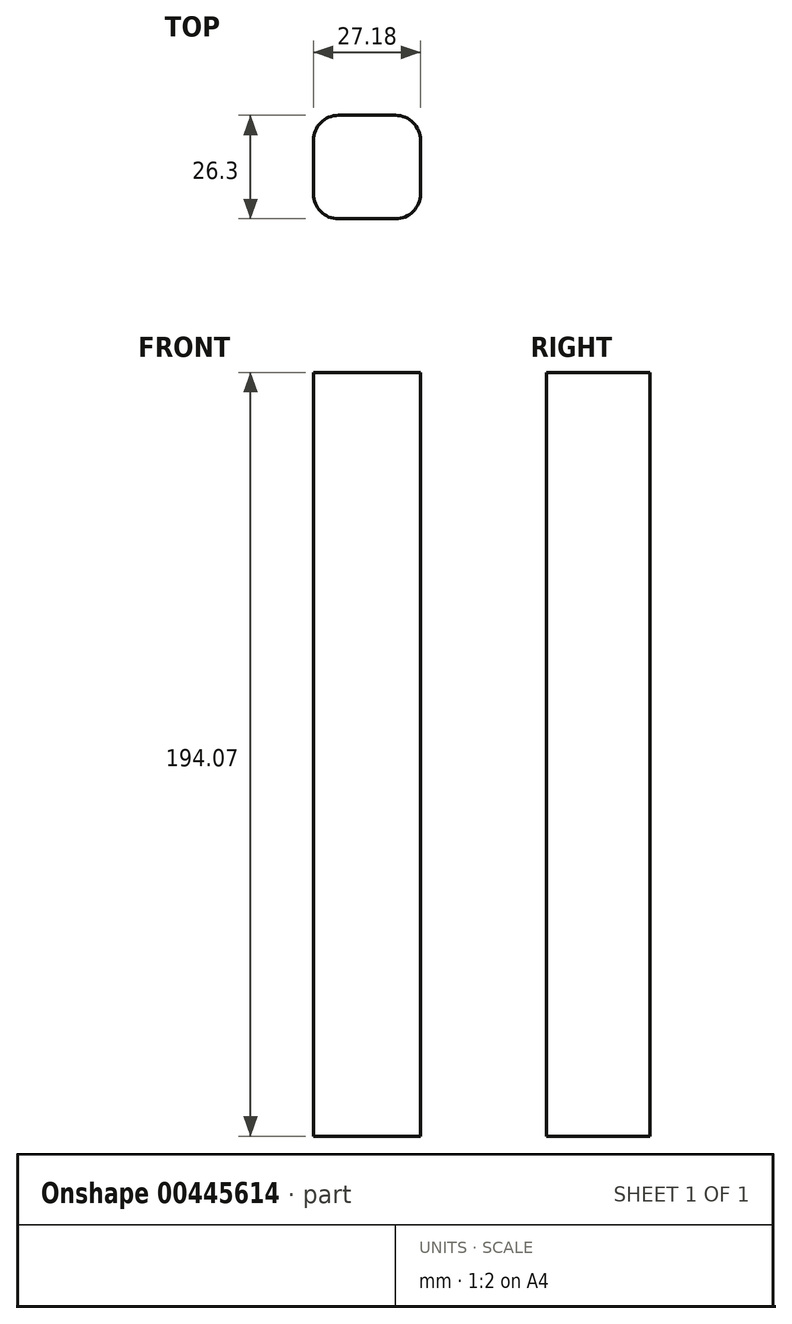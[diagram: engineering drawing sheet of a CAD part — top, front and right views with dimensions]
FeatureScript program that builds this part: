
annotation { "Feature Type Name" : "Feature", "Feature Type Description" : "" }
export const myFeature = defineFeature(function(context is Context, id is Id, definition is map)
    precondition{}
    {
        {
            var Q0;
            Q0=qCreatedBy(makeId("Right.planeOp"),FACE);
            var sketch = newSketch(context, id + "F0", { "sketchPlane" : qUnion([Q0])});
            skLineSegment(sketch, "E0.bottom", {"start": v(-3.37, 72.65) * mm, "end": v(3.37, 72.65) * mm});
            skLineSegment(sketch, "E0.top", {"start": v(-3.37, -72.65) * mm, "end": v(3.37, -72.65) * mm});
            skLineSegment(sketch, "E0.left", {"start": v(-3.37, 72.65) * mm, "end": v(-3.37, -72.65) * mm});
            skLineSegment(sketch, "E0.right", {"start": v(3.37, 72.65) * mm, "end": v(3.37, -72.65) * mm});
            skPoint(sketch, "E0.middle", {"position": v(0, 0) * mm});
            skSolve(sketch);
        }
        {
            var Q0;
            Q0=makeQuery(id+"F0.imprint","IMPRINT",FACE,{"disambiguationData":[TD([[makeQuery(id+"F0.imprint","IMPRINT",EDGE,{"derivedFrom":sQuery(id+"F0.wireOp",EDGE,"E0.bottom")}),-1.0]])]});
            extrude(context, id + "F1", {"entities" : qUnion([Q0]), "depth" : 9.65 * mm});
        }
        {
            var Q0;
            Q0=makeQuery(id+"F1.opExtrude","SWEPT_FACE",FACE,{"disambiguationData":[OSD([sQuery(id+"F0.wireOp",EDGE,"E0.left")])]});
            extrude(context, id + "F2", {"entities" : qUnion([Q0]), "operationType" : NewBodyOperationType.ADD, "depth" : 3.3 * mm});
        }
        {
            var Q0;
            {var subQ0=sQuery(id+"F0.wireOp",EDGE,"E0.top");Q0=makeQuery(id+"F2.boolean.opBoolean","MERGE",FACE,{"derivedFrom":[makeQuery(id+"F1.opExtrude","SWEPT_FACE",FACE,{"disambiguationData":[OSD([subQ0])]}),makeQuery(id+"F2.opExtrude","SWEPT_FACE",FACE,{"disambiguationData":[OSD([subQ0,sQuery(id+"F0.wireOp",EDGE,"E0.left")])]})]});}
            extrude(context, id + "F3", {"entities" : qUnion([Q0]), "operationType" : NewBodyOperationType.ADD, "depth" : 48.77 * mm});
        }
        {
            var Q0;
            {var subQ0=sQuery(id+"F0.wireOp",EDGE,"E0.left");var subQ1=sQuery(id+"F0.wireOp",EDGE,"E0.top");Q0=makeQuery(id+"F3.boolean.opBoolean","MERGE",FACE,{"derivedFrom":[makeQuery(id+"F2.boolean.opBoolean","MERGE",FACE,{"derivedFrom":[makeQuery(id+"F1.opExtrude","CAP_FACE",FACE,{"disambiguationData":[OSD([sQuery(id+"F0.wireOp",EDGE,"E0.bottom"),subQ1,subQ0,sQuery(id+"F0.wireOp",EDGE,"E0.right")])],"isStart":false}),makeQuery(id+"F2.opExtrude","SWEPT_FACE",FACE,{"disambiguationData":[OSD([subQ0]),TDD([makeQuery(id+"F1.opExtrude","CAP_EDGE",EDGE,{"disambiguationData":[OSD([subQ0])],"isStart":false})])]})]}),makeQuery(id+"F3.opExtrude","SWEPT_FACE",FACE,{"disambiguationData":[OSD([subQ1,subQ0]),TDD([makeQuery(id+"F2.boolean.opBoolean","MERGE",EDGE,{"derivedFrom":[makeQuery(id+"F1.opExtrude","CAP_EDGE",EDGE,{"disambiguationData":[OSD([subQ1])],"isStart":false}),makeQuery(id+"F2.opExtrude","SWEPT_EDGE",EDGE,{"disambiguationData":[OSD([subQ1,subQ0]),TDD([makeQuery(id+"F1.opExtrude","CAP_VERTEX",VERTEX,{"disambiguationData":[OSD([subQ1,subQ0])],"isStart":false})])]})]})])]})]});}
            extrude(context, id + "F4", {"entities" : qUnion([Q0]), "operationType" : NewBodyOperationType.ADD, "depth" : 17.53 * mm});
        }
        {
            var Q0;
            {var subQ0=sQuery(id+"F0.wireOp",EDGE,"E0.left");var subQ1=sQuery(id+"F0.wireOp",EDGE,"E0.top");Q0=makeQuery(id+"F4.boolean.opBoolean","MERGE",FACE,{"derivedFrom":[makeQuery(id+"F3.boolean.opBoolean","MERGE",FACE,{"derivedFrom":[makeQuery(id+"F2.opExtrude","CAP_FACE",FACE,{"disambiguationData":[OSD([subQ0])],"isStart":false}),makeQuery(id+"F3.opExtrude","SWEPT_FACE",FACE,{"disambiguationData":[OSD([subQ1,subQ0]),TDD([makeQuery(id+"F2.opExtrude","CAP_EDGE",EDGE,{"disambiguationData":[OSD([subQ1,subQ0])],"isStart":false})])]})]}),makeQuery(id+"F4.opExtrude","SWEPT_FACE",FACE,{"disambiguationData":[OSD([subQ1,subQ0]),TDD([makeQuery(id+"F3.boolean.opBoolean","MERGE",EDGE,{"derivedFrom":[makeQuery(id+"F2.opExtrude","CAP_EDGE",EDGE,{"disambiguationData":[OSD([subQ0]),TDD([makeQuery(id+"F1.opExtrude","CAP_EDGE",EDGE,{"disambiguationData":[OSD([subQ0])],"isStart":false})])],"isStart":false}),makeQuery(id+"F3.opExtrude","SWEPT_EDGE",EDGE,{"disambiguationData":[OSD([subQ1,subQ0]),TDD([makeQuery(id+"F2.opExtrude","CAP_VERTEX",VERTEX,{"disambiguationData":[OSD([subQ1,subQ0]),TDD([makeQuery(id+"F1.opExtrude","CAP_VERTEX",VERTEX,{"disambiguationData":[OSD([subQ1,subQ0])],"isStart":false})])],"isStart":false})])]})]})])]})]});}
            extrude(context, id + "F5", {"entities" : qUnion([Q0]), "operationType" : NewBodyOperationType.ADD, "depth" : 16.26 * mm});
        }
        {
            var Q0;
            {var subQ0=sQuery(id+"F0.wireOp",EDGE,"E0.left");var subQ1=sQuery(id+"F0.wireOp",EDGE,"E0.top");Q0=makeQuery(id+"F5.opExtrude","CAP_EDGE",EDGE,{"disambiguationData":[OSD([subQ1,subQ0]),TDD([makeQuery(id+"F4.opExtrude","CAP_EDGE",EDGE,{"disambiguationData":[OSD([subQ1,subQ0]),TDD([makeQuery(id+"F3.boolean.opBoolean","MERGE",EDGE,{"derivedFrom":[makeQuery(id+"F2.opExtrude","CAP_EDGE",EDGE,{"disambiguationData":[OSD([subQ0]),TDD([makeQuery(id+"F1.opExtrude","CAP_EDGE",EDGE,{"disambiguationData":[OSD([subQ0])],"isStart":false})])],"isStart":false}),makeQuery(id+"F3.opExtrude","SWEPT_EDGE",EDGE,{"disambiguationData":[OSD([subQ1,subQ0]),TDD([makeQuery(id+"F2.opExtrude","CAP_VERTEX",VERTEX,{"disambiguationData":[OSD([subQ1,subQ0]),TDD([makeQuery(id+"F1.opExtrude","CAP_VERTEX",VERTEX,{"disambiguationData":[OSD([subQ1,subQ0])],"isStart":false})])],"isStart":false})])]})]})])],"isStart":false})])],"isStart":false});}
            fillet(context, id + "F6", {"entities" : qUnion([Q0]), "radius" : 6.35 * mm, "tangentPropagation" : true, "allowEdgeOverflow" : false});
        }
        {
            var Q0;
            Q0=makeQuery(id+"F4.opExtrude","CAP_EDGE",EDGE,{"disambiguationData":[OSD([sQuery(id+"F0.wireOp",EDGE,"E0.top"),sQuery(id+"F0.wireOp",EDGE,"E0.right")])],"isStart":false});
            fillet(context, id + "F7", {"entities" : qUnion([Q0]), "radius" : 6.35 * mm, "tangentPropagation" : true, "allowEdgeOverflow" : false});
        }
        {
            var Q0;
            {var subQ0=sQuery(id+"F0.wireOp",EDGE,"E0.left");var subQ1=sQuery(id+"F0.wireOp",EDGE,"E0.top");Q0=makeQuery(id+"F5.opExtrude","CAP_EDGE",EDGE,{"disambiguationData":[OSD([subQ1,subQ0]),TDD([makeQuery(id+"F3.boolean.opBoolean","MERGE",EDGE,{"derivedFrom":[makeQuery(id+"F2.opExtrude","CAP_EDGE",EDGE,{"disambiguationData":[OSD([subQ0]),TDD([makeQuery(id+"F1.opExtrude","CAP_EDGE",EDGE,{"disambiguationData":[OSD([subQ0])],"isStart":true})])],"isStart":false}),makeQuery(id+"F3.opExtrude","SWEPT_EDGE",EDGE,{"disambiguationData":[OSD([subQ1,subQ0]),TDD([makeQuery(id+"F2.opExtrude","CAP_VERTEX",VERTEX,{"disambiguationData":[OSD([subQ1,subQ0]),TDD([makeQuery(id+"F1.opExtrude","CAP_VERTEX",VERTEX,{"disambiguationData":[OSD([subQ1,subQ0])],"isStart":true})])],"isStart":false})])]})]})])],"isStart":false});}
            var Q1;
            {var subQ0=sQuery(id+"F0.wireOp",EDGE,"E0.right");var subQ1=sQuery(id+"F0.wireOp",EDGE,"E0.top");Q1=makeQuery(id+"F3.boolean.opBoolean","MERGE",EDGE,{"derivedFrom":[makeQuery(id+"F1.opExtrude","CAP_EDGE",EDGE,{"disambiguationData":[OSD([subQ0])],"isStart":true}),makeQuery(id+"F3.opExtrude","SWEPT_EDGE",EDGE,{"disambiguationData":[OSD([subQ1,subQ0]),TDD([makeQuery(id+"F1.opExtrude","CAP_VERTEX",VERTEX,{"disambiguationData":[OSD([subQ1,subQ0])],"isStart":true})])]})]});}
            fillet(context, id + "F8", {"entities" : qUnion([Q0, Q1]), "radius" : 6.35 * mm, "tangentPropagation" : true, "allowEdgeOverflow" : false});
        }
    });
